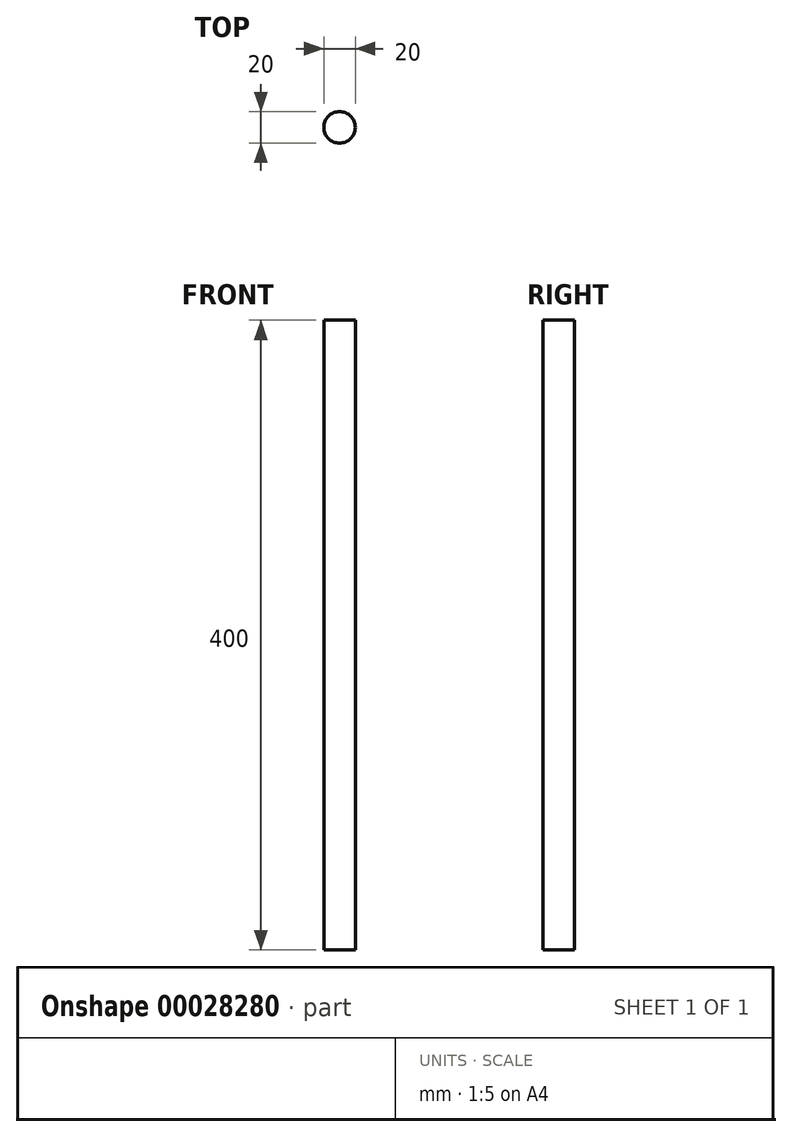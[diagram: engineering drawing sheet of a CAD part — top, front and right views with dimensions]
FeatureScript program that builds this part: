
annotation { "Feature Type Name" : "Feature", "Feature Type Description" : "" }
export const myFeature = defineFeature(function(context is Context, id is Id, definition is map)
    precondition{}
    {
        {
            var Q0;
            Q0=qCreatedBy(makeId("Top.planeOp"),FACE);
            var sketch = newSketch(context, id + "F0", { "sketchPlane" : qUnion([Q0])});
            skCircle(sketch, "E0", {"center": v(0, 0) * mm, "radius": 10 * mm});
            skSolve(sketch);
        }
        {
            var Q0;
            Q0 = qSketchRegion(id + "F0", true);
            extrude(context, id + "F1", {"entities" : qUnion([Q0]), "depth" : 400 * mm});
        }
    });
